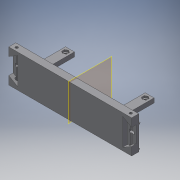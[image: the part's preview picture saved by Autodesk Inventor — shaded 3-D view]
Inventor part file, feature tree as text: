
AUTODESK INVENTOR PART (.ipt)
format: ipt  version: 2016 SP2 (Build 200236200, 236)  size: 223,744 bytes
history: native  units: mm
features: reference x17, sketch x8, extrude x7, mirror x1, plane x1
ambient origin geometry x8: Origin, YZ Plane, XZ Plane, XY Plane, X Axis, Y Axis, Z Axis, Center Point
bodies: Volumenkörper1 (feature_tree)
feature tree (34):
  extrude  "Extrusion1"  Depth=0.1mm
  extrude  "Extrusion2"  Depth=35.0mm TaperAngle=0.0deg
  extrude  "Extrusion3"  Depth=1.0mm
  extrude  "Extrusion12"  Depth=1.0mm TaperAngle=0.0deg
  extrude  "Extrusion13"  Depth=12.55mm
  extrude  "Extrusion14"  Depth=5.0mm
  extrude  "Extrusion15"  Depth=36.75mm
  mirror  "Spiegeln3"
  plane  "Arbeitsebene1"
  sketch  "Skizze15"  dims[d60=5.0mm d61=5.0mm d62=5.0mm d63=0.0mm d64=5.7mm d65=2.2mm d66=0.0mm]
  sketch  "Skizze1"  dims[d0=69.4mm d1=0.0mm d7=0.1mm]
  reference  "Referenz1"
  reference  "Referenz2"
  reference  "Referenz3"
  reference  "Referenz4"
  reference  "Referenz5"
  reference  "Referenz6"
  reference  "Referenz8"
  reference  "Referenz9"
  sketch  "Skizze2"  dims[d8=5.0mm d9=0.0mm d10=35.0mm d11=0.0mm]
  sketch  "Skizze3"  dims[d19=2.0mm d20=1.0mm]
  reference  "Referenz10"
  reference  "Referenz11"
  reference  "Referenz12"
  reference  "Referenz13"
  reference  "Referenz14"
  sketch  "Skizze11"  dims[d21=1.0mm d51=4.45mm d52=0.0mm]
  reference  "Referenz19"
  reference  "Referenz20"
  reference  "Referenz21"
  reference  "Referenz22"
  sketch  "Skizze12"  dims[d53=19.4mm d54=12.55mm]
  sketch  "Skizze13"  dims[d55=10.0mm d56=5.0mm]
  sketch  "Skizze14"  dims[d57=36.75mm d58=0.0mm d59=3.1mm]
